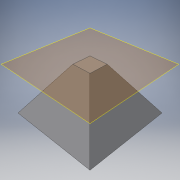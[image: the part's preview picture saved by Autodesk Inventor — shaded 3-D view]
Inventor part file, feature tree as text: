
AUTODESK INVENTOR PART (.ipt)
format: ipt  version: 2016 (Build 200138000, 138)  size: 99,328 bytes
history: native  units: in
note: dims shown in document units (in); Inventor stores cm internally (conversion verified against a paired STEP export)
features: sketch x2, plane x1, loft x1, shell x1
ambient origin geometry x8: Origin, YZ Plane, XZ Plane, XY Plane, X Axis, Y Axis, Z Axis, Center Point
bodies: Solid1 (feature_tree)
feature tree (5):
  sketch  "Sketch1"  dims[d0=11.75in d1=11.75in d2=6.5in]
  plane  "Work Plane1"
  loft  "Loft1"
  shell  "Shell1"  Thickness=6.5in
  sketch  "Sketch2"  dims[d3=2.5in d4=2.5in d5=0.0in d6=90.0deg d7=0.0in d8=90.0deg d9=0.1in]
